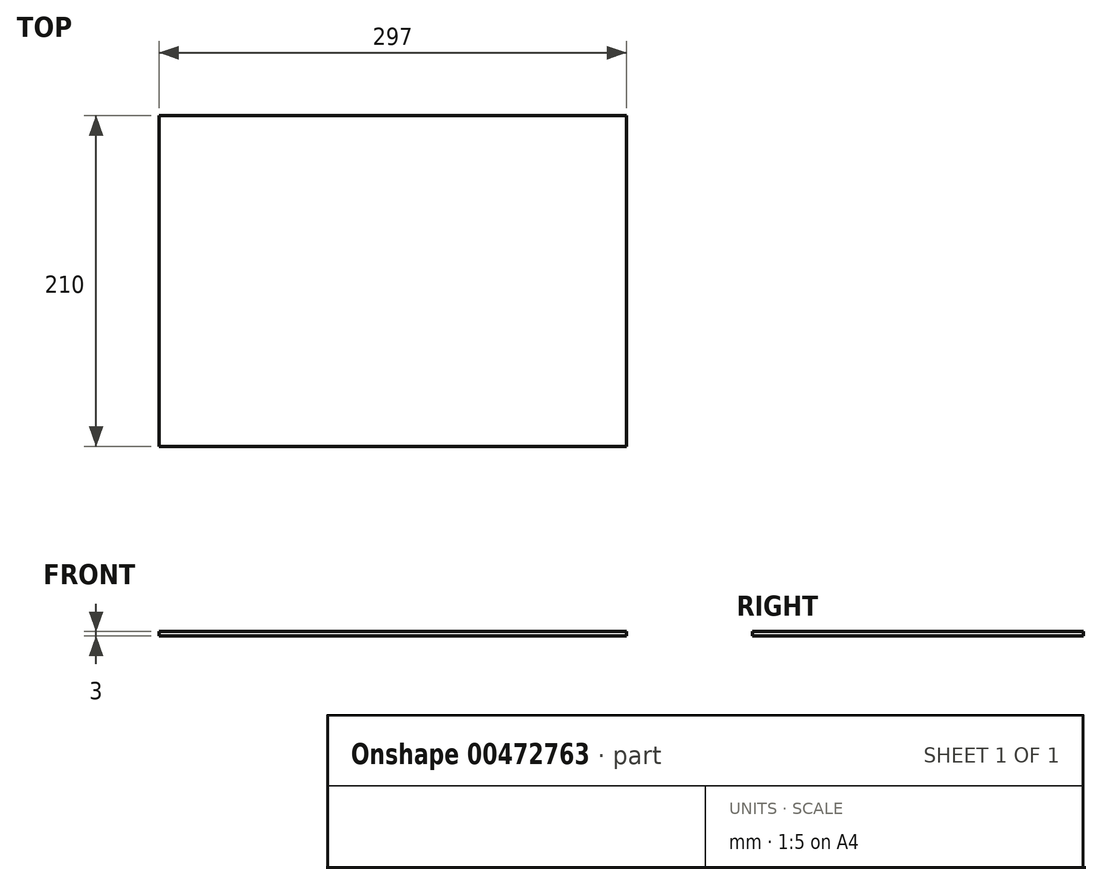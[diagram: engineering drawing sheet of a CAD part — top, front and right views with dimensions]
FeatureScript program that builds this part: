
annotation { "Feature Type Name" : "Feature", "Feature Type Description" : "" }
export const myFeature = defineFeature(function(context is Context, id is Id, definition is map)
    precondition{}
    {
        {
            assignVariable(context, id + "F0", {"name" : "e", "anyValue" : 3});
        }
        {
            var Q0;
            Q0=qCreatedBy(makeId("Top.planeOp"),FACE);
            var sketch = newSketch(context, id + "F1", { "sketchPlane" : qUnion([Q0])});
            skLineSegment(sketch, "E0.bottom", {"start": v(0, 0) * mm, "end": v(297, 0) * mm});
            skLineSegment(sketch, "E0.top", {"start": v(0, 210) * mm, "end": v(297, 210) * mm});
            skLineSegment(sketch, "E0.left", {"start": v(0, 0) * mm, "end": v(0, 210) * mm});
            skLineSegment(sketch, "E0.right", {"start": v(297, 0) * mm, "end": v(297, 210) * mm});
            skSolve(sketch);
        }
        {
            var Q0;
            Q0 = qSketchRegion(id + "F1", true);
            extrude(context, id + "F2", {"entities" : qUnion([Q0]), "offsetDistance" : 25 * mm, "depth" : (getVariable(context, 'e')) * mm});
        }
    });
